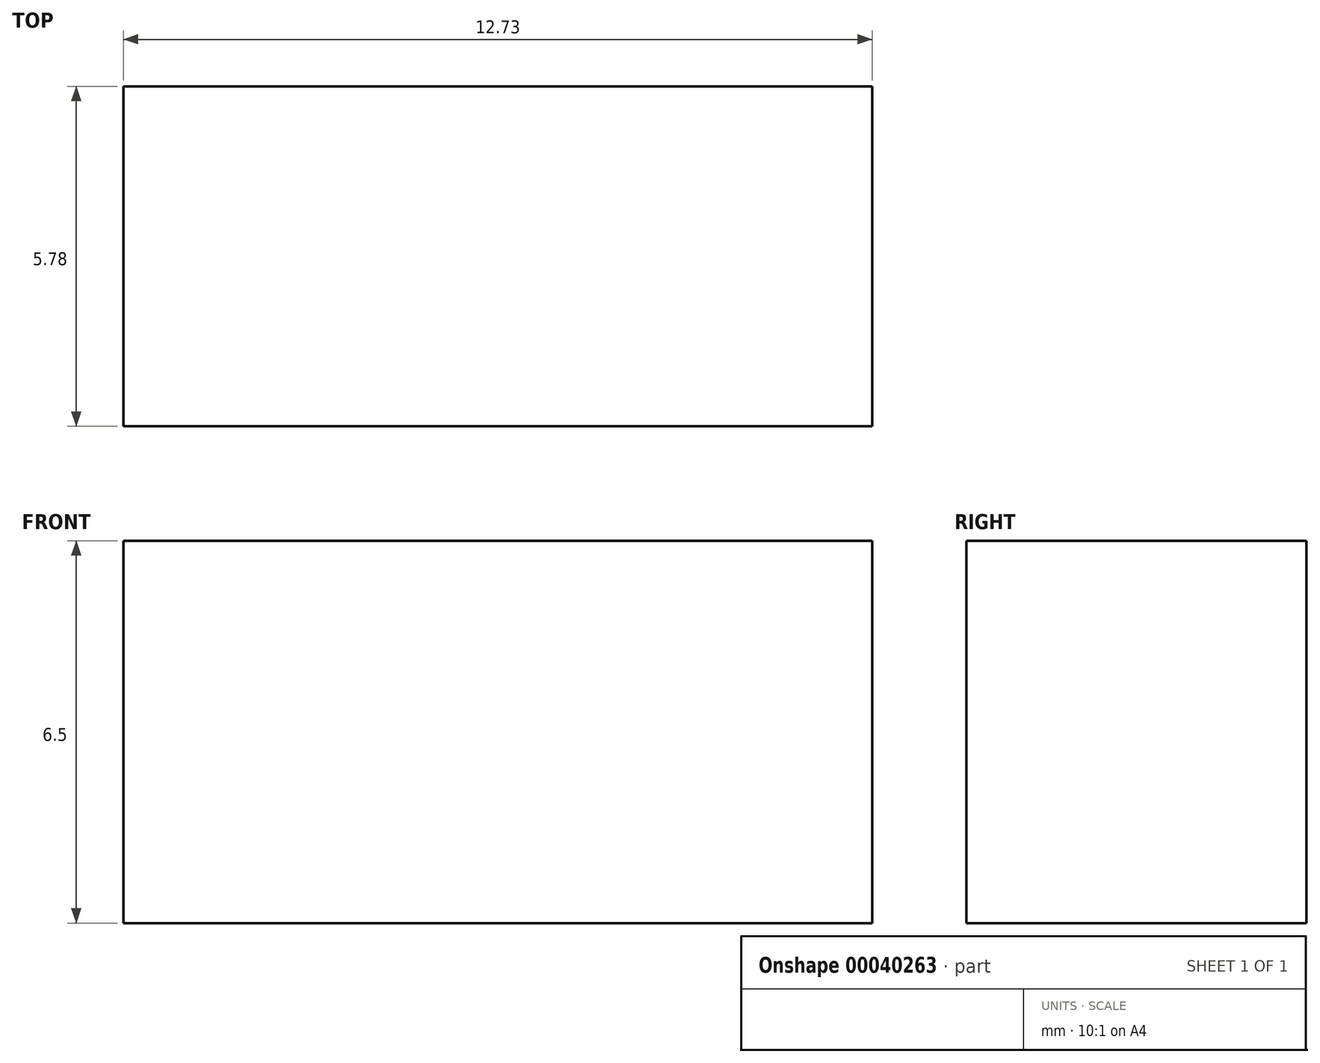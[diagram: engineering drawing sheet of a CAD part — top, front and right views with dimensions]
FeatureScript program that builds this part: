
annotation { "Feature Type Name" : "Feature", "Feature Type Description" : "" }
export const myFeature = defineFeature(function(context is Context, id is Id, definition is map)
    precondition{}
    {
        {
            var Q0;
            Q0=qCreatedBy(makeId("Front.planeOp"),FACE);
            var sketch = newSketch(context, id + "F0", { "sketchPlane" : qUnion([Q0])});
            skLineSegment(sketch, "E0.bottom", {"start": v(0, 0) * mm, "end": v(12.73, 0) * mm});
            skLineSegment(sketch, "E0.top", {"start": v(0, 6.5) * mm, "end": v(12.73, 6.5) * mm});
            skLineSegment(sketch, "E0.left", {"start": v(0, 0) * mm, "end": v(0, 6.5) * mm});
            skLineSegment(sketch, "E0.right", {"start": v(12.73, 0) * mm, "end": v(12.73, 6.5) * mm});
            skSolve(sketch);
        }
        {
            var Q0;
            Q0=makeQuery(id+"F0.imprint","IMPRINT",FACE,{"disambiguationData":[TD([[makeQuery(id+"F0.imprint","IMPRINT",EDGE,{"derivedFrom":sQuery(id+"F0.wireOp",EDGE,"E0.bottom")}),1.0]])]});
            extrude(context, id + "F1", {"entities" : qUnion([Q0]), "depth" : 5.78 * mm});
        }
    });
